# Revit family: WCT_A3-Durowin-1511x2134-DDAH
name_source: partatom
category: Doors
revit_build: Autodesk Revit 2016 (Build: 20150220_1215(x64)
units: mm (PartAtom-declared; Revit-internal decimal feet)

## family parameters
Always vertical = Yes
Cut with Voids When Loaded = No
Host = Wall
Room Calculation Point = No
Shared = No

## types (1)
- DDAH Durowin
    Assembly Code = B2030120
    Construction Type = Steel
    Frame Width = 22 mm  [stored 0.0721785 ft]
    Function = Interior
    Height = 2134 mm  [stored 7.00131 ft]
    Manufacturer = Durowin
    Manufacturer Code = DDAH
    Material Door Frame = Default Steel Door Frame
    Material Door Panel = Default Steel Door Panel
    Material Glass = Glass
    Model = French Door And Sidelights
    Model Type = Butt Hinge
    Panel Width = 756 mm
    Rough Height = 2156 mm
    Rough Width = 1555 mm
    Thickness = 0 mm  [stored 0 ft]
    URL = http://www.Durowin.com
    Wall Closure = By host
    Width = 1511 mm

note: [stored X ft] marks values corroborated as IEEE doubles in the binary element streams (Revit-internal decimal feet)

## geometry (parser evidence)
native form markers: Sweep x4
no freeform markers — native parametric forms only
